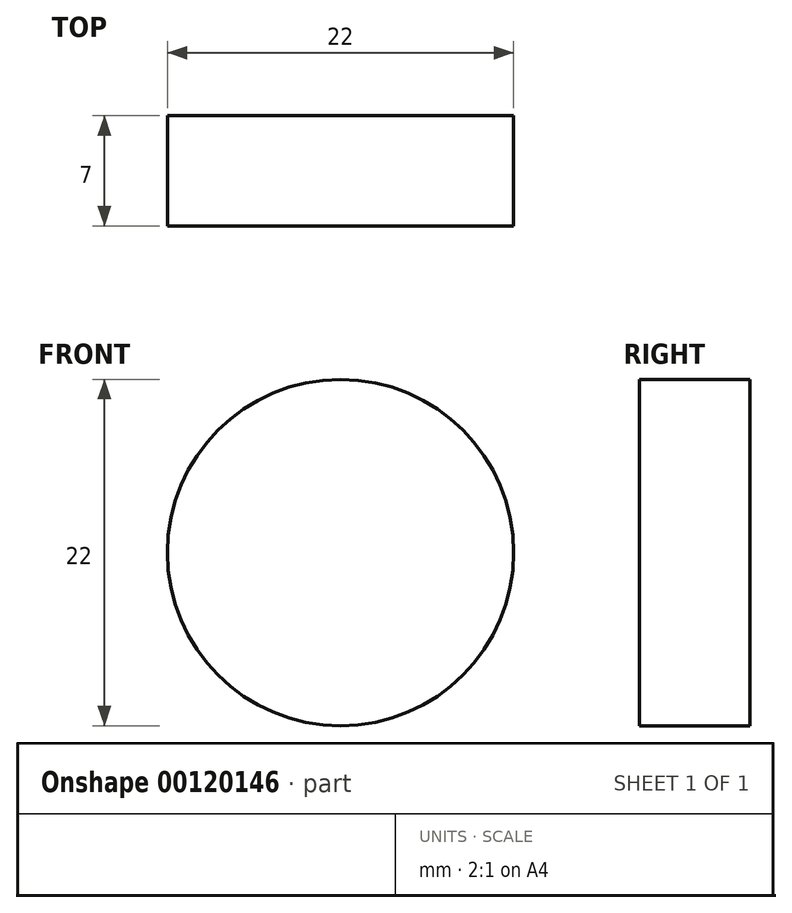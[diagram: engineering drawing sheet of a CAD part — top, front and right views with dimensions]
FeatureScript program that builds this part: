
annotation { "Feature Type Name" : "Feature", "Feature Type Description" : "" }
export const myFeature = defineFeature(function(context is Context, id is Id, definition is map)
    precondition{}
    {
        {
            var Q0;
            Q0=qCreatedBy(makeId("Front.planeOp"),FACE);
            var sketch = newSketch(context, id + "F0", { "sketchPlane" : qUnion([Q0])});
            skCircle(sketch, "E0", {"center": v(0, 0) * mm, "radius": 11 * mm});
            skSolve(sketch);
        }
        {
            var Q0;
            Q0 = qSketchRegion(id + "F0", true);
            extrude(context, id + "F1", {"entities" : qUnion([Q0]), "depth" : 7 * mm});
        }
    });
